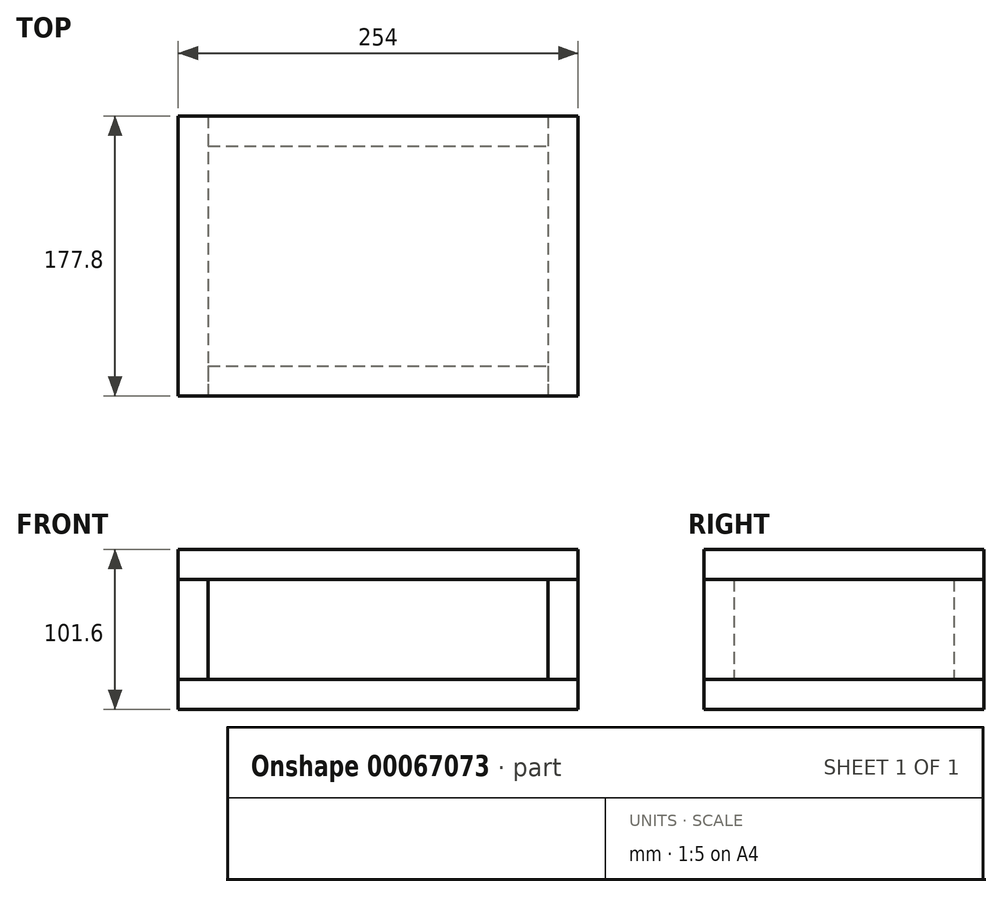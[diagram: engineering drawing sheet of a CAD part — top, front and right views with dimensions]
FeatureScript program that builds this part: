
annotation { "Feature Type Name" : "Feature", "Feature Type Description" : "" }
export const myFeature = defineFeature(function(context is Context, id is Id, definition is map)
    precondition{}
    {
        {
            var Q0;
            Q0=qCreatedBy(makeId("Top.planeOp"),FACE);
            var sketch = newSketch(context, id + "F0", { "sketchPlane" : qUnion([Q0])});
            skLineSegment(sketch, "E0.bottom", {"start": v(0, 0) * mm, "end": v(254, 0) * mm});
            skLineSegment(sketch, "E0.top", {"start": v(0, 177.8) * mm, "end": v(254, 177.8) * mm});
            skLineSegment(sketch, "E0.left", {"start": v(0, 0) * mm, "end": v(0, 177.8) * mm});
            skLineSegment(sketch, "E0.right", {"start": v(254, 0) * mm, "end": v(254, 177.8) * mm});
            skSolve(sketch);
        }
        {
            var Q0;
            Q0 = qSketchRegion(id + "F0", true);
            extrude(context, id + "F1", {"entities" : qUnion([Q0]), "depth" : 19.05 * mm});
        }
        {
            var Q0;
            Q0=makeQuery(id+"F1.opExtrude","CAP_FACE",FACE,{"disambiguationData":[OSD([sQuery(id+"F0.wireOp",EDGE,"E0.bottom"),sQuery(id+"F0.wireOp",EDGE,"E0.top"),sQuery(id+"F0.wireOp",EDGE,"E0.left"),sQuery(id+"F0.wireOp",EDGE,"E0.right")])],"isStart":false});
            var sketch = newSketch(context, id + "F2", { "sketchPlane" : qUnion([Q0])});
            skLineSegment(sketch, "E1.bottom", {"start": v(0, 177.8) * mm, "end": v(19.05, 177.8) * mm});
            skLineSegment(sketch, "E1.top", {"start": v(0, 0) * mm, "end": v(19.05, 0) * mm});
            skLineSegment(sketch, "E1.left", {"start": v(0, 177.8) * mm, "end": v(0, 0) * mm});
            skLineSegment(sketch, "E1.right", {"start": v(19.05, 177.8) * mm, "end": v(19.05, 0) * mm});
            skLineSegment(sketch, "E2.bottom", {"start": v(254, 177.8) * mm, "end": v(234.95, 177.8) * mm});
            skLineSegment(sketch, "E2.top", {"start": v(254, 0) * mm, "end": v(234.95, 0) * mm});
            skLineSegment(sketch, "E2.left", {"start": v(254, 177.8) * mm, "end": v(254, 0) * mm});
            skLineSegment(sketch, "E2.right", {"start": v(234.95, 177.8) * mm, "end": v(234.95, 0) * mm});
            skLineSegment(sketch, "E3.bottom", {"start": v(19.05, 0) * mm, "end": v(234.95, 0) * mm});
            skLineSegment(sketch, "E3.top", {"start": v(19.05, 19.05) * mm, "end": v(234.95, 19.05) * mm});
            skLineSegment(sketch, "E3.left", {"start": v(19.05, 0) * mm, "end": v(19.05, 19.05) * mm});
            skLineSegment(sketch, "E3.right", {"start": v(234.95, 0) * mm, "end": v(234.95, 19.05) * mm});
            skLineSegment(sketch, "E4.bottom", {"start": v(19.05, 177.8) * mm, "end": v(234.95, 177.8) * mm});
            skLineSegment(sketch, "E4.top", {"start": v(19.05, 158.75) * mm, "end": v(234.95, 158.75) * mm});
            skLineSegment(sketch, "E4.left", {"start": v(19.05, 177.8) * mm, "end": v(19.05, 158.75) * mm});
            skLineSegment(sketch, "E4.right", {"start": v(234.95, 177.8) * mm, "end": v(234.95, 158.75) * mm});
            skSolve(sketch);
        }
        {
            var Q0;
            Q0=makeQuery(id+"F2.imprint","IMPRINT",FACE,{"disambiguationData":[TD([[makeQuery(id+"F2.imprint","IMPRINT",EDGE,{"derivedFrom":sQuery(id+"F2.wireOp",EDGE,"E1.bottom")}),-1.0]])]});
            var Q1;
            Q1=makeQuery(id+"F2.imprint","IMPRINT",FACE,{"disambiguationData":[TD([[makeQuery(id+"F2.imprint","IMPRINT",EDGE,{"derivedFrom":sQuery(id+"F2.wireOp",EDGE,"E2.bottom")}),-1.0]])]});
            extrude(context, id + "F3", {"entities" : qUnion([Q0, Q1]), "depth" : 63.5 * mm});
        }
        {
            var Q0;
            Q0=makeQuery(id+"F2.imprint","IMPRINT",FACE,{"disambiguationData":[TD([[makeQuery(id+"F2.imprint","IMPRINT",EDGE,{"derivedFrom":sQuery(id+"F2.wireOp",EDGE,"E3.bottom")}),1.0]])]});
            var Q1;
            Q1=makeQuery(id+"F2.imprint","IMPRINT",FACE,{"disambiguationData":[TD([[makeQuery(id+"F2.imprint","IMPRINT",EDGE,{"derivedFrom":sQuery(id+"F2.wireOp",EDGE,"E4.bottom")}),-1.0]])]});
            extrude(context, id + "F4", {"entities" : qUnion([Q0, Q1]), "depth" : 63.5 * mm});
        }
        {
            var Q0;
            Q0=makeQuery(id+"F3.opExtrude","CAP_FACE",FACE,{"disambiguationData":[OSD([sQuery(id+"F2.wireOp",EDGE,"E1.bottom"),sQuery(id+"F2.wireOp",EDGE,"E1.top"),sQuery(id+"F2.wireOp",EDGE,"E1.left"),sQuery(id+"F2.wireOp",EDGE,"E1.right"),sQuery(id+"F2.wireOp",EDGE,"E3.left"),sQuery(id+"F2.wireOp",EDGE,"E4.left")])],"isStart":false});
            var sketch = newSketch(context, id + "F5", { "sketchPlane" : qUnion([Q0])});
            skLineSegment(sketch, "E5.0.0", {"start": v(19.05, 0) * mm, "end": v(19.05, 177.8) * mm});
            skLineSegment(sketch, "E5.0.1", {"start": v(19.05, 177.8) * mm, "end": v(0, 177.8) * mm});
            skLineSegment(sketch, "E5.0.2", {"start": v(0, 177.8) * mm, "end": v(0, 0) * mm});
            skLineSegment(sketch, "E5.0.3", {"start": v(0, 0) * mm, "end": v(19.05, 0) * mm});
            skLineSegment(sketch, "E6.0", {"start": v(19.05, 177.8) * mm, "end": v(234.95, 177.8) * mm});
            skLineSegment(sketch, "E7.0", {"start": v(254, 0) * mm, "end": v(254, 177.8) * mm});
            skLineSegment(sketch, "E8.0", {"start": v(19.05, 0) * mm, "end": v(234.95, 0) * mm});
            skLineSegment(sketch, "E9.bottom", {"start": v(0, 177.8) * mm, "end": v(254, 177.8) * mm});
            skLineSegment(sketch, "E9.top", {"start": v(0, 0) * mm, "end": v(254, 0) * mm});
            skLineSegment(sketch, "E9.right", {"start": v(254, 177.8) * mm, "end": v(254, 0) * mm});
            skSolve(sketch);
        }
        {
            var Q0;
            Q0 = qSketchRegion(id + "F5", true);
            extrude(context, id + "F6", {"entities" : qUnion([Q0]), "depth" : 19.05 * mm});
        }
    });
